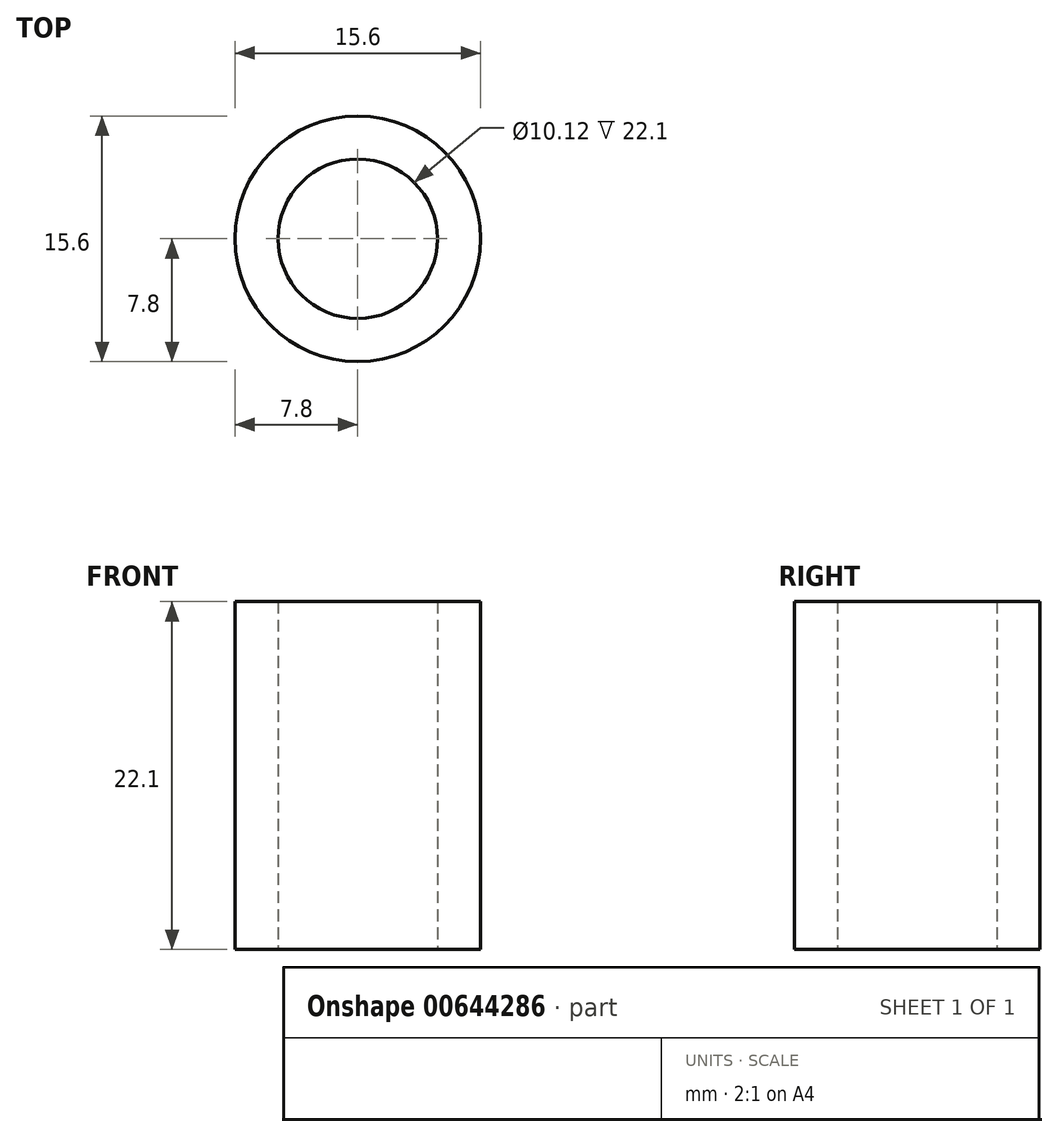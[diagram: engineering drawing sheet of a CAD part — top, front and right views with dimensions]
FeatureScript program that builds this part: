
annotation { "Feature Type Name" : "Feature", "Feature Type Description" : "" }
export const myFeature = defineFeature(function(context is Context, id is Id, definition is map)
    precondition{}
    {
        {
            var Q0;
            Q0=qCreatedBy(makeId("Top.planeOp"),FACE);
            var sketch = newSketch(context, id + "F0", { "sketchPlane" : qUnion([Q0])});
            skCircle(sketch, "E0", {"center": v(0, 0) * mm, "radius": 5.06 * mm});
            skCircle(sketch, "E1", {"center": v(0, 0) * mm, "radius": 7.8 * mm});
            skSolve(sketch);
        }
        {
            var Q0;
            Q0=makeQuery(id+"F0.imprint","IMPRINT",FACE,{"disambiguationData":[TD([[makeQuery(id+"F0.imprint","IMPRINT",EDGE,{"derivedFrom":sQuery(id+"F0.wireOp",EDGE,"E0")}),-1.0]])]});
            extrude(context, id + "F1", {"entities" : qUnion([Q0]), "depth" : 22.1 * mm, "offsetDistance" : 25 * mm});
        }
    });
